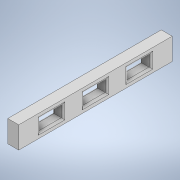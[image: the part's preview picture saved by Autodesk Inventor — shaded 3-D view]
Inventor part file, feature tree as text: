
AUTODESK INVENTOR PART (.ipt)
format: ipt  version: 2020 (Build 240168000, 168)  size: 155,648 bytes
history: native  units: mm
features: extrude x2, sketch x2, fillet x1
ambient origin geometry x8: Origin, YZ Plane, XZ Plane, XY Plane, X Axis, Y Axis, Z Axis, Center Point
bodies: Solid1 (feature_tree)
feature tree (5):
  extrude  "Extrusion1"  Depth=42.0mm
  extrude  "Extrusion2"  TaperAngle=0.0deg  [1 undecoded]
  fillet  "Fillet1"  Radius=6.3mm
  sketch  "Sketch1"  dims[d0=6.0mm d1=42.0mm]
  sketch  "Sketch2"  dims[d2=3.0mm d3=0.0mm d4=6.3mm d5=3.3mm d6=5.85mm d7=30.0mm d9=12.0mm d10=10.0mm d12=10.0mm d14=3.0mm d15=0.0mm d16=5.85mm d17=0.5mm]
note: 1 required parameter value undecoded (feature->parameter linkage not recoverable at this tier; creation-order binding heuristic only, values carry confidence <= 0.55)
